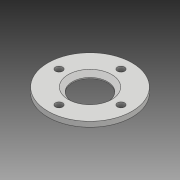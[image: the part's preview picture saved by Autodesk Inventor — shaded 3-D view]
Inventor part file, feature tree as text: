
AUTODESK INVENTOR PART (.ipt)
format: ipt  version: 2018 (Build 220112000, 112)  size: 206,336 bytes
history: native  units: mm
features: extrude x2, sketch x2, other x1, pattern_circular x1, chamfer x1
ambient origin geometry x8: Origin, YZ Plane, XZ Plane, XY Plane, X Axis, Y Axis, Z Axis, Center Point
bodies: Body1 (feature_tree)
feature tree (7):
  other  "ソリッド1"
  extrude  "押し出し1"  Depth=40.7mm
  extrude  "押し出し2"  Depth=17.0mm
  pattern_circular  "円形状パターン1"  [2 undecoded]
  chamfer  "面取り1"  Distance=15.0mm
  sketch  "スケッチ1"
  sketch  "スケッチ2"
note: 2 required parameter values undecoded (feature->parameter linkage not recoverable at this tier; creation-order binding heuristic only, values carry confidence <= 0.55)
